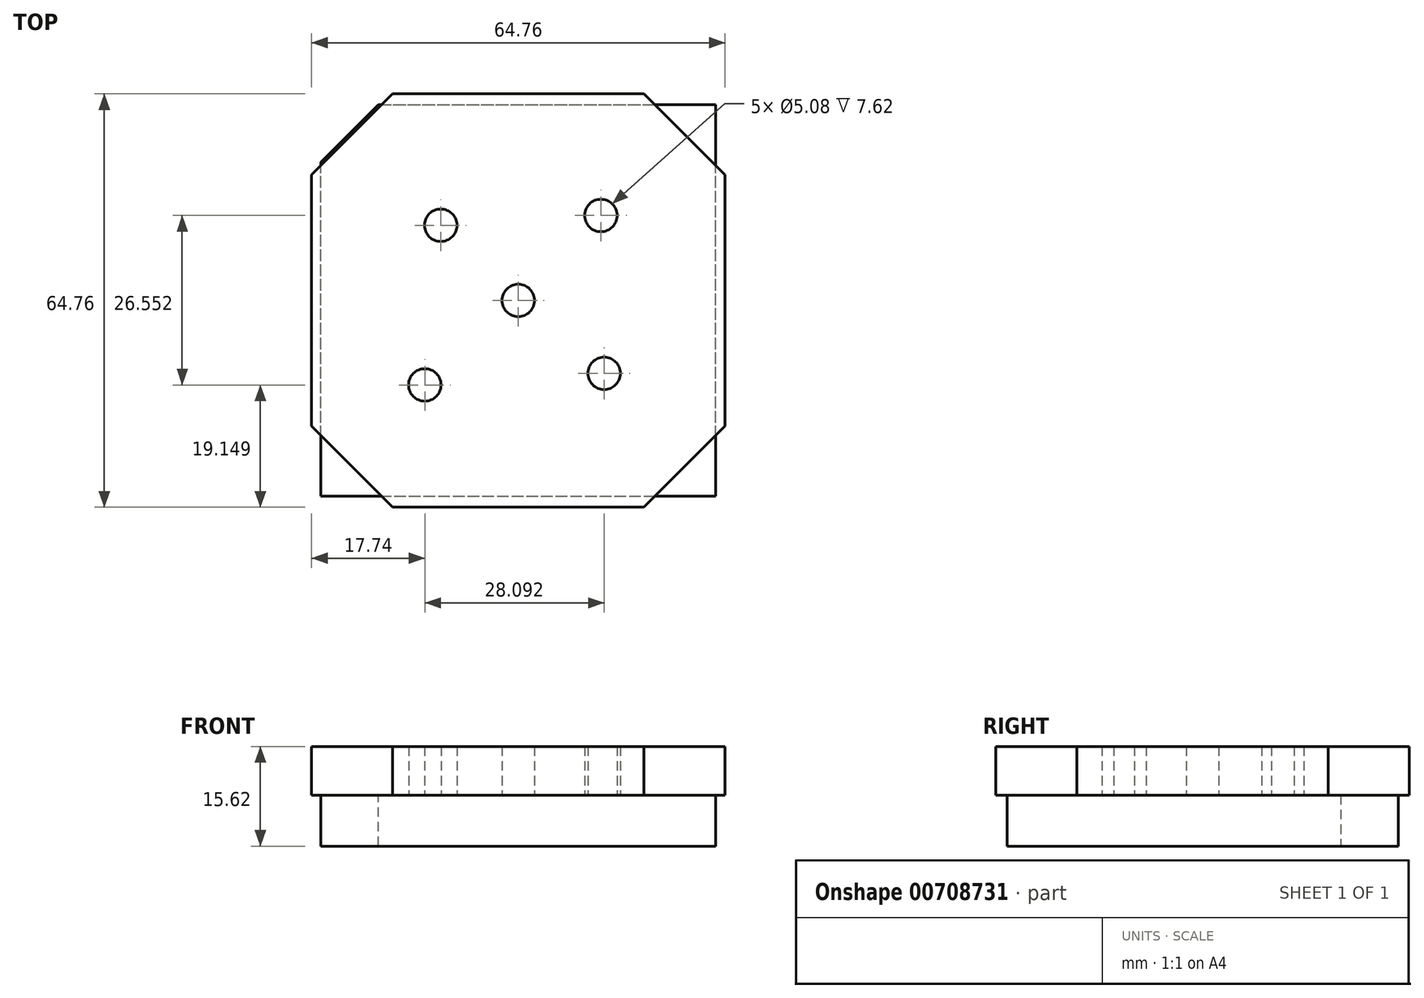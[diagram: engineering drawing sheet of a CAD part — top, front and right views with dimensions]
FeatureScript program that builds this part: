
annotation { "Feature Type Name" : "Feature", "Feature Type Description" : "" }
export const myFeature = defineFeature(function(context is Context, id is Id, definition is map)
    precondition{}
    {
        {
            var Q0;
            Q0=qCreatedBy(makeId("Top.planeOp"),FACE);
            var sketch = newSketch(context, id + "F0", { "sketchPlane" : qUnion([Q0])});
            skLineSegment(sketch, "E0.bottom", {"start": v(-32.38, 32.38) * mm, "end": v(32.38, 32.38) * mm});
            skLineSegment(sketch, "E0.top", {"start": v(-32.38, -32.38) * mm, "end": v(32.38, -32.38) * mm});
            skLineSegment(sketch, "E0.left", {"start": v(-32.38, 32.38) * mm, "end": v(-32.38, -32.38) * mm});
            skLineSegment(sketch, "E0.right", {"start": v(32.38, 32.38) * mm, "end": v(32.38, -32.38) * mm});
            skPoint(sketch, "E0.middle", {"position": v(0, 0) * mm});
            skSolve(sketch);
        }
        {
            var Q0;
            Q0=makeQuery(id+"F0.imprint","IMPRINT",FACE,{"disambiguationData":[TD([[makeQuery(id+"F0.imprint","IMPRINT",EDGE,{"derivedFrom":sQuery(id+"F0.wireOp",EDGE,"E0.bottom")}),-1.0]])]});
            extrude(context, id + "F1", {"entities" : qUnion([Q0]), "depth" : 7.62 * mm, "offsetDistance" : 25.4 * mm});
        }
        {
            var Q0;
            Q0=makeQuery(id+"F1.opExtrude","SWEPT_EDGE",EDGE,{"disambiguationData":[OSD([sQuery(id+"F0.wireOp",EDGE,"E0.top"),sQuery(id+"F0.wireOp",EDGE,"E0.right")])]});
            chamfer(context, id + "F2", {"entities" : qUnion([Q0]), "width" : 12.7 * mm, "tangentPropagation" : true});
        }
        {
            var Q0;
            Q0=makeQuery(id+"F1.opExtrude","SWEPT_EDGE",EDGE,{"disambiguationData":[OSD([sQuery(id+"F0.wireOp",EDGE,"E0.bottom"),sQuery(id+"F0.wireOp",EDGE,"E0.left")])]});
            chamfer(context, id + "F3", {"entities" : qUnion([Q0]), "width" : 12.7 * mm, "tangentPropagation" : true});
        }
        {
            var Q0;
            Q0=makeQuery(id+"F1.opExtrude","SWEPT_EDGE",EDGE,{"disambiguationData":[OSD([sQuery(id+"F0.wireOp",EDGE,"E0.top"),sQuery(id+"F0.wireOp",EDGE,"E0.left")])]});
            chamfer(context, id + "F4", {"entities" : qUnion([Q0]), "width" : 12.7 * mm, "tangentPropagation" : true});
        }
        {
            var Q0;
            Q0=makeQuery(id+"F1.opExtrude","SWEPT_EDGE",EDGE,{"disambiguationData":[OSD([sQuery(id+"F0.wireOp",EDGE,"E0.bottom"),sQuery(id+"F0.wireOp",EDGE,"E0.right")])]});
            chamfer(context, id + "F5", {"entities" : qUnion([Q0]), "width" : 12.7 * mm, "tangentPropagation" : true});
        }
        {
            var Q0;
            Q0=qCreatedBy(makeId("Top.planeOp"),FACE);
            var sketch = newSketch(context, id + "F6", { "sketchPlane" : qUnion([Q0])});
            skLineSegment(sketch, "E1.bottom", {"start": v(-30.94, -30.65) * mm, "end": v(30.94, -30.65) * mm});
            skLineSegment(sketch, "E1.top", {"start": v(-30.94, 30.65) * mm, "end": v(30.94, 30.65) * mm});
            skLineSegment(sketch, "E1.left", {"start": v(-30.94, -30.65) * mm, "end": v(-30.94, 30.65) * mm});
            skLineSegment(sketch, "E1.right", {"start": v(30.94, -30.65) * mm, "end": v(30.94, 30.65) * mm});
            skPoint(sketch, "E1.middle", {"position": v(0, 0) * mm});
            skSolve(sketch);
        }
        {
            var Q0;
            Q0=makeQuery(id+"FVWPBNdpcpUA1jo_1.boolean.opBoolean","MERGE",FACE,{"derivedFrom":[makeQuery(id+"F1.opExtrude","CAP_FACE",FACE,{"disambiguationData":[OSD([sQuery(id+"F0.wireOp",EDGE,"E0.bottom"),sQuery(id+"F0.wireOp",EDGE,"E0.top"),sQuery(id+"F0.wireOp",EDGE,"E0.left"),sQuery(id+"F0.wireOp",EDGE,"E0.right")])],"isStart":true}),makeQuery(id+"FVWPBNdpcpUA1jo_1.opExtrude","CAP_FACE",FACE,{"disambiguationData":[OSD([sQuery(id+"F6.wireOp",EDGE,"E1.bottom"),sQuery(id+"F6.wireOp",EDGE,"E1.top"),sQuery(id+"F6.wireOp",EDGE,"E1.left"),sQuery(id+"F6.wireOp",EDGE,"E1.right")])],"isStart":true})]});
            var sketch = newSketch(context, id + "F7", { "sketchPlane" : qUnion([Q0])});
            skCircle(sketch, "E2", {"center": v(12.94, -13.32) * mm, "radius": 7.7 * mm});
            skSolve(sketch);
        }
        {
            var Q0;
            Q0=makeQuery(id+"F7.imprint","IMPRINT",FACE,{"disambiguationData":[TD([[makeQuery(id+"F7.imprint","IMPRINT",EDGE,{"derivedFrom":sQuery(id+"F7.wireOp",EDGE,"E2")}),-1.0]])]});
            var sketch = newSketch(context, id + "F8", { "sketchPlane" : qUnion([Q0])});
            skCircle(sketch, "E3", {"center": v(0, 0) * mm, "radius": 7.37 * mm});
            skSolve(sketch);
        }
        {
            var Q0;
            Q0=makeQuery(id+"F8.imprint","IMPRINT",FACE,{"disambiguationData":[TD([[makeQuery(id+"F8.imprint","IMPRINT",EDGE,{"derivedFrom":sQuery(id+"F8.wireOp",EDGE,"E3")}),-1.0]])]});
            var sketch = newSketch(context, id + "F9", { "sketchPlane" : qUnion([Q0])});
            skCircle(sketch, "E4", {"center": v(-14.64, 13.23) * mm, "radius": 8.13 * mm});
            skSolve(sketch);
        }
        {
            var Q0;
            Q0=makeQuery(id+"F7.imprint","IMPRINT",FACE,{"disambiguationData":[TD([[makeQuery(id+"F7.imprint","IMPRINT",EDGE,{"derivedFrom":sQuery(id+"F7.wireOp",EDGE,"E2")}),-1.0]])]});
            var sketch = newSketch(context, id + "F10", { "sketchPlane" : qUnion([Q0])});
            skCircle(sketch, "E5", {"center": v(13.45, 11.41) * mm, "radius": 7.27 * mm});
            skSolve(sketch);
        }
        {
            var Q0;
            Q0=makeQuery(id+"F7.imprint","IMPRINT",FACE,{"disambiguationData":[TD([[makeQuery(id+"F7.imprint","IMPRINT",EDGE,{"derivedFrom":sQuery(id+"F7.wireOp",EDGE,"E2")}),-1.0]])]});
            var sketch = newSketch(context, id + "F11", { "sketchPlane" : qUnion([Q0])});
            skCircle(sketch, "E6", {"center": v(-12.16, -11.79) * mm, "radius": 7.06 * mm});
            skSolve(sketch);
        }
        {
            var Q0;
            Q0=sQuery(id+"F10.wireOp",VERTEX,"E5.center");
            var Q1;
            Q1=makeQuery(id+"F1.opExtrude","SWEPT_BODY",BODY,{"disambiguationData":[OSD([sQuery(id+"F0.wireOp",EDGE,"E0.bottom"),sQuery(id+"F0.wireOp",EDGE,"E0.top"),sQuery(id+"F0.wireOp",EDGE,"E0.left"),sQuery(id+"F0.wireOp",EDGE,"E0.right")])]});
            hole(context, id + "F12", {"style" : HoleStyle.SIMPLE, "endStyle" : HoleEndStyle.THROUGH, "holeDiameter" : 5.08 * mm, "majorDiameter" : 6.35 * mm, "isTappedThrough" : true, "tappedDepth" : 12.7 * mm, "tapClearance" : 3, "locations" : qUnion([Q0]), "scope" : qUnion([Q1])});
        }
        {
            var Q0;
            Q0=sQuery(id+"F7.wireOp",VERTEX,"E2.center");
            var Q1;
            Q1=makeQuery(id+"F1.opExtrude","SWEPT_BODY",BODY,{"disambiguationData":[OSD([sQuery(id+"F0.wireOp",EDGE,"E0.bottom"),sQuery(id+"F0.wireOp",EDGE,"E0.top"),sQuery(id+"F0.wireOp",EDGE,"E0.left"),sQuery(id+"F0.wireOp",EDGE,"E0.right")])]});
            hole(context, id + "F13", {"style" : HoleStyle.SIMPLE, "endStyle" : HoleEndStyle.THROUGH, "holeDiameter" : 5.08 * mm, "majorDiameter" : 6.35 * mm, "isTappedThrough" : true, "tappedDepth" : 12.7 * mm, "tapClearance" : 3, "locations" : qUnion([Q0]), "scope" : qUnion([Q1])});
        }
        {
            var Q0;
            Q0=sQuery(id+"F8.wireOp",VERTEX,"E3.center");
            var Q1;
            Q1=makeQuery(id+"F1.opExtrude","SWEPT_BODY",BODY,{"disambiguationData":[OSD([sQuery(id+"F0.wireOp",EDGE,"E0.bottom"),sQuery(id+"F0.wireOp",EDGE,"E0.top"),sQuery(id+"F0.wireOp",EDGE,"E0.left"),sQuery(id+"F0.wireOp",EDGE,"E0.right")])]});
            hole(context, id + "F14", {"style" : HoleStyle.SIMPLE, "endStyle" : HoleEndStyle.THROUGH, "holeDiameter" : 5.08 * mm, "majorDiameter" : 6.35 * mm, "isTappedThrough" : true, "tappedDepth" : 12.7 * mm, "tapClearance" : 3, "locations" : qUnion([Q0]), "scope" : qUnion([Q1])});
        }
        {
            var Q0;
            Q0=sQuery(id+"F11.wireOp",VERTEX,"E6.center");
            var Q1;
            Q1=sQuery(id+"F9.wireOp",VERTEX,"E4.center");
            var Q2;
            Q2=makeQuery(id+"F1.opExtrude","SWEPT_BODY",BODY,{"disambiguationData":[OSD([sQuery(id+"F0.wireOp",EDGE,"E0.bottom"),sQuery(id+"F0.wireOp",EDGE,"E0.top"),sQuery(id+"F0.wireOp",EDGE,"E0.left"),sQuery(id+"F0.wireOp",EDGE,"E0.right")])]});
            hole(context, id + "F15", {"style" : HoleStyle.SIMPLE, "endStyle" : HoleEndStyle.THROUGH, "holeDiameter" : 5.08 * mm, "majorDiameter" : 6.35 * mm, "isTappedThrough" : true, "tappedDepth" : 12.7 * mm, "tapClearance" : 3, "locations" : qUnion([Q0, Q1]), "scope" : qUnion([Q2])});
        }
        {
            var Q0;
            Q0 = qSketchRegion(id + "F6", true);
            extrude(context, id + "F16", {"entities" : qUnion([Q0]), "operationType" : NewBodyOperationType.ADD, "oppositeDirection" : true, "depth" : 8 * mm, "offsetDistance" : 25 * mm});
        }
        {
            var Q0;
            Q0=makeQuery(id+"F16.opExtrude","SWEPT_EDGE",EDGE,{"disambiguationData":[OSD([sQuery(id+"F6.wireOp",EDGE,"E1.top"),sQuery(id+"F6.wireOp",EDGE,"E1.left")])]});
            chamfer(context, id + "F17", {"entities" : qUnion([Q0]), "width" : 9 * mm, "tangentPropagation" : true});
        }
    });
